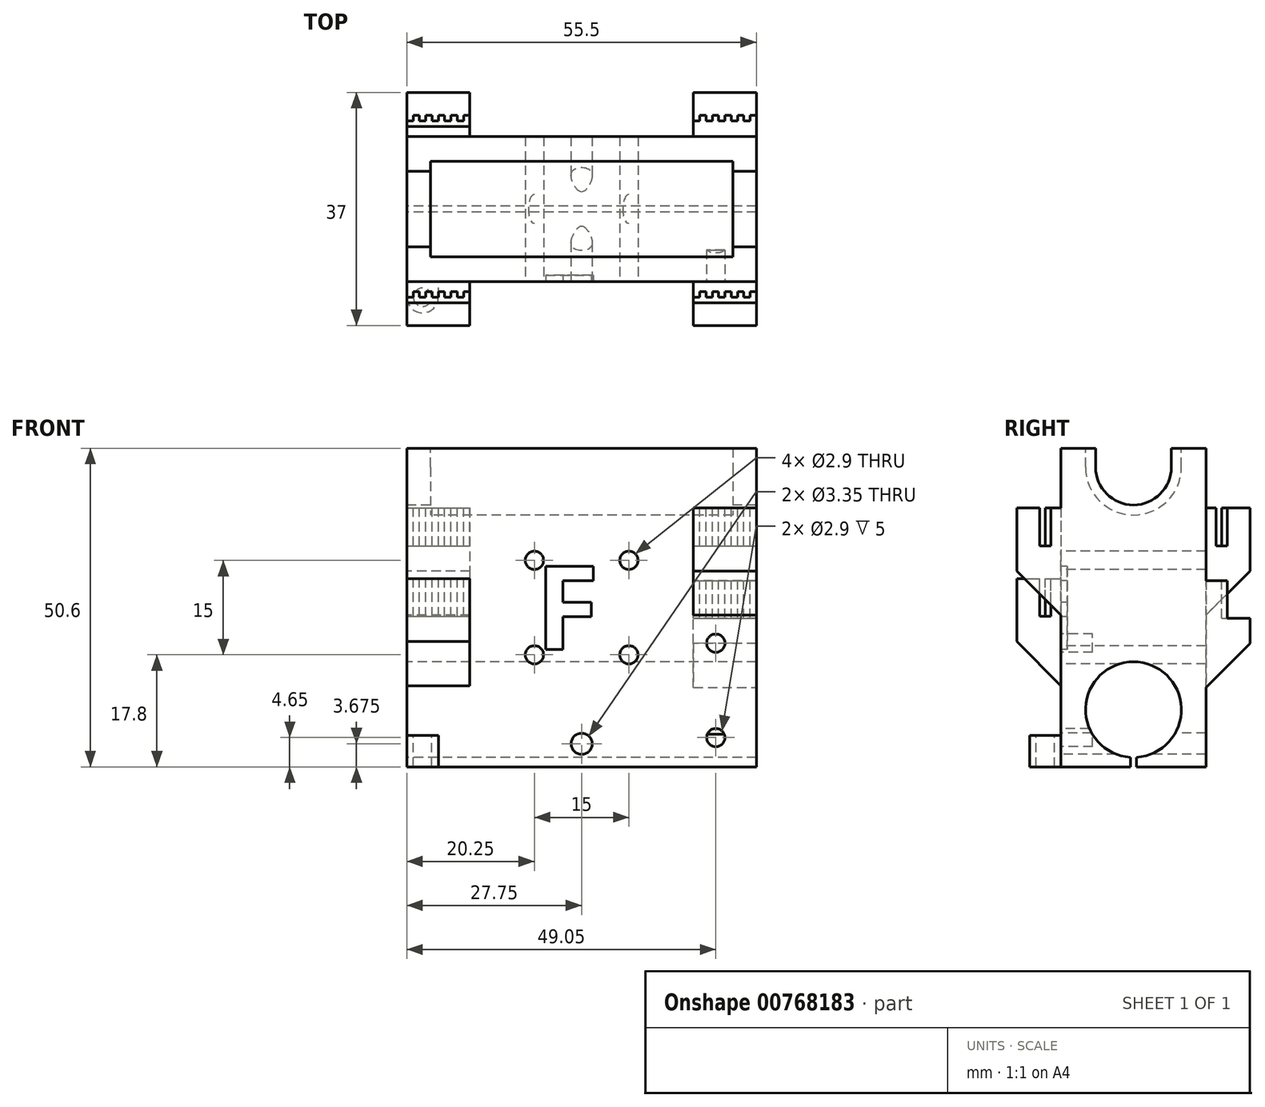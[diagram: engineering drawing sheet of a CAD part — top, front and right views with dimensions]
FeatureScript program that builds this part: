
annotation { "Feature Type Name" : "Feature", "Feature Type Description" : "" }
export const myFeature = defineFeature(function(context is Context, id is Id, definition is map)
    precondition{}
    {
        {
            assignVariable(context, id + "F0", {"name" : "LM8LUU", "anyValue" : 2.75});
        }
        {
            var Q0;
            Q0=qCreatedBy(makeId("Top.planeOp"),FACE);
            var sketch = newSketch(context, id + "F1", { "sketchPlane" : qUnion([Q0])});
            skLineSegment(sketch, "E0.bottom", {"start": v(0, 0) * mm, "end": v(55.5, 0) * mm});
            skLineSegment(sketch, "E0.top", {"start": v(0, 23) * mm, "end": v(55.5, 23) * mm});
            skLineSegment(sketch, "E0.left", {"start": v(0, 0) * mm, "end": v(0, 23) * mm});
            skLineSegment(sketch, "E0.right", {"start": v(55.5, 0) * mm, "end": v(55.5, 23) * mm});
            skSolve(sketch);
        }
        {
            var Q0;
            Q0=qSketchRegion(id+"F1",true);
            extrude(context, id + "F2", {"entities" : qUnion([Q0]), "depth" : 50.6 * mm});
        }
        {
            var Q0;
            Q0=makeQuery(id+"F2.opExtrude","SWEPT_FACE",FACE,{"disambiguationData":[OSD([sQuery(id+"F1.wireOp",EDGE,"E0.left")])]});
            var sketch = newSketch(context, id + "F3", { "sketchPlane" : qUnion([Q0])});
            skCircle(sketch, "E1", {"center": v(-11.5, 9.1) * mm, "radius": 7.6 * mm});
            skCircle(sketch, "E2", {"center": v(-11.5, 47.6) * mm, "radius": 6 * mm});
            skLineSegment(sketch, "E3", {"start": v(-23, 47.6) * mm, "end": v(0, 47.6) * mm, "construction": true});
            skLineSegment(sketch, "E4", {"start": v(-17.5, 50.6) * mm, "end": v(-17.5, 47.6) * mm});
            skLineSegment(sketch, "E5", {"start": v(-5.5, 50.6) * mm, "end": v(-5.5, 47.6) * mm});
            skLineSegment(sketch, "E6", {"start": v(-23, 9.1) * mm, "end": v(0, 9.1) * mm, "construction": true});
            skLineSegment(sketch, "E7", {"start": v(-11.5, 9.1) * mm, "end": v(-11.5, 0) * mm, "construction": true});
            skLineSegment(sketch, "E8", {"start": v(-11.5, 0) * mm, "end": v(-12, 0) * mm});
            skLineSegment(sketch, "E9", {"start": v(-12, 0) * mm, "end": v(-12, 1.52) * mm});
            skLineSegment(sketch, "E10", {"start": v(-12, 1.52) * mm, "end": v(-11, 1.52) * mm});
            skLineSegment(sketch, "E11", {"start": v(-11, 1.52) * mm, "end": v(-11, 0) * mm});
            skLineSegment(sketch, "E12", {"start": v(-11, 0) * mm, "end": v(-11.5, 0) * mm});
            skLineSegment(sketch, "E13", {"start": v(-11.5, 15.6) * mm, "end": v(-11.5, 16.7) * mm});
            skLineSegment(sketch, "E14", {"start": v(-11.5, 15.6) * mm, "end": v(-7, 15.22) * mm});
            skLineSegment(sketch, "E15", {"start": v(-11.5, 15.6) * mm, "end": v(-16, 15.22) * mm});
            skCircle(sketch, "E16", {"center": v(-11.5, 47.6) * mm, "radius": 7.6 * mm});
            skLineSegment(sketch, "E17", {"start": v(-3.9, 47.6) * mm, "end": v(-3.9, 50.6) * mm});
            skLineSegment(sketch, "E18", {"start": v(-19.1, 47.6) * mm, "end": v(-19.1, 50.6) * mm});
            skSolve(sketch);
        }
        {
            var Q0;
            {var subQ0=sQuery(id+"F3.wireOp",EDGE,"E14");var subQ1=sQuery(id+"F3.wireOp",EDGE,"E1");var subQ3=makeQuery(id+"F3.imprint","INTERSECT",VERTEX,{"disambiguationData":[OD(0.0)],"derivedFrom":[subQ1,subQ0]});Q0=makeQuery(id+"F3.imprint","IMPRINT",FACE,{"disambiguationData":[TD([[makeQuery(id+"F3.imprint","IMPRINT",EDGE,{"disambiguationData":[TD([[subQ3,-1.0]])],"derivedFrom":subQ1}),1.0]])]});}
            var Q1;
            {var subQ0=sQuery(id+"F3.wireOp",EDGE,"E15");var subQ1=sQuery(id+"F3.wireOp",EDGE,"E1");var subQ3=makeQuery(id+"F3.imprint","INTERSECT",VERTEX,{"disambiguationData":[OD(0.0)],"derivedFrom":[subQ1,subQ0]});Q1=makeQuery(id+"F3.imprint","IMPRINT",FACE,{"disambiguationData":[TD([[makeQuery(id+"F3.imprint","IMPRINT",EDGE,{"disambiguationData":[TD([[subQ3,1.0]])],"derivedFrom":subQ1}),1.0]])]});}
            var Q2;
            Q2=makeQuery(id+"F3.imprint","IMPRINT",FACE,{"disambiguationData":[TD([[makeQuery(id+"F3.imprint","IMPRINT",EDGE,{"derivedFrom":sQuery(id+"F3.wireOp",EDGE,"E8")}),-1.0]])]});
            var Q3;
            {var subQ0=sQuery(id+"F3.wireOp",EDGE,"E10");Q3=makeQuery(id+"F3.imprint","IMPRINT",FACE,{"disambiguationData":[TD([[makeQuery(id+"F3.imprint","IMPRINT",EDGE,{"derivedFrom":subQ0}),-1.0]])]});}
            var Q4;
            {var subQ3=sQuery(id+"F3.wireOp",EDGE,"E13");Q4=makeQuery(id+"F3.imprint","IMPRINT",FACE,{"disambiguationData":[TD([[makeQuery(id+"F3.imprint","IMPRINT",EDGE,{"derivedFrom":subQ3}),-1.0]])]});}
            var Q5;
            {var subQ3=sQuery(id+"F3.wireOp",EDGE,"E13");Q5=makeQuery(id+"F3.imprint","IMPRINT",FACE,{"disambiguationData":[TD([[makeQuery(id+"F3.imprint","IMPRINT",EDGE,{"derivedFrom":subQ3}),1.0]])]});}
            var Q6;
            {var subQ7=sQuery(id+"F3.wireOp",EDGE,"E10");Q6=makeQuery(id+"F3.imprint","IMPRINT",FACE,{"disambiguationData":[TD([[makeQuery(id+"F3.imprint","IMPRINT",EDGE,{"derivedFrom":subQ7}),1.0]])]});}
            var Q7;
            {var subQ3=sQuery(id+"F3.wireOp",EDGE,"E5");Q7=makeQuery(id+"F3.imprint","IMPRINT",FACE,{"disambiguationData":[TD([[makeQuery(id+"F3.imprint","IMPRINT",EDGE,{"derivedFrom":subQ3}),-1.0]])]});}
            var Q8;
            {var subQ0=sQuery(id+"F3.wireOp",EDGE,"E4");Q8=makeQuery(id+"F3.imprint","IMPRINT",FACE,{"disambiguationData":[TD([[makeQuery(id+"F3.imprint","IMPRINT",EDGE,{"derivedFrom":subQ0}),1.0]])]});}
            var Q9;
            {var subQ0=sQuery(id+"F3.wireOp",EDGE,"E4");Q9=makeQuery(id+"F3.imprint","IMPRINT",FACE,{"disambiguationData":[TD([[makeQuery(id+"F3.imprint","IMPRINT",EDGE,{"derivedFrom":subQ0}),1.0]])]});}
            var Q10;
            {var subQ3=sQuery(id+"F3.wireOp",EDGE,"E5");Q10=makeQuery(id+"F3.imprint","IMPRINT",FACE,{"disambiguationData":[TD([[makeQuery(id+"F3.imprint","IMPRINT",EDGE,{"derivedFrom":subQ3}),-1.0]])]});}
            var Q11;
            {var subQ1=sQuery(id+"F3.wireOp",EDGE,"E2");var subQ4=makeQuery(id+"F3.imprint","INTERSECT",VERTEX,{"derivedFrom":[subQ1,sQuery(id+"F3.wireOp",EDGE,"E5")]});Q11=makeQuery(id+"F3.imprint","IMPRINT",FACE,{"disambiguationData":[TD([[makeQuery(id+"F3.imprint","IMPRINT",EDGE,{"disambiguationData":[TD([[subQ4,-1.0]])],"derivedFrom":subQ1}),1.0]])]});}
            extrude(context, id + "F4", {"entities" : qUnion([Q0, Q1, Q2, Q3, Q4, Q5, Q6, Q7, Q8, Q9, Q10, Q11]), "operationType" : NewBodyOperationType.REMOVE, "endBound" : BoundingType.THROUGH_ALL, "oppositeDirection" : true, "depth" : 25 * mm});
        }
        {
            var Q0;
            {var subQ3=sQuery(id+"F3.wireOp",EDGE,"E4");Q0=makeQuery(id+"F3.imprint","IMPRINT",FACE,{"disambiguationData":[TD([[makeQuery(id+"F3.imprint","IMPRINT",EDGE,{"derivedFrom":subQ3}),-1.0]])]});}
            var Q1;
            {var subQ3=sQuery(id+"F3.wireOp",EDGE,"E18");Q1=makeQuery(id+"F3.imprint","IMPRINT",FACE,{"disambiguationData":[TD([[makeQuery(id+"F3.imprint","IMPRINT",EDGE,{"derivedFrom":subQ3}),-1.0]])]});}
            var Q2;
            {var subQ3=sQuery(id+"F3.wireOp",EDGE,"E17");Q2=makeQuery(id+"F3.imprint","IMPRINT",FACE,{"disambiguationData":[TD([[makeQuery(id+"F3.imprint","IMPRINT",EDGE,{"derivedFrom":subQ3}),1.0]])]});}
            extrude(context, id + "F5", {"entities" : qUnion([Q0, Q1, Q2]), "operationType" : NewBodyOperationType.REMOVE, "oppositeDirection" : true, "depth" : (46.25 + getVariable(context, 'LM8LUU') * 2) * mm, "offsetDistance" : 25 * mm});
        }
        {
            var Q0;
            {var subQ3=sQuery(id+"F3.wireOp",EDGE,"E4");Q0=makeQuery(id+"F3.imprint","IMPRINT",FACE,{"disambiguationData":[TD([[makeQuery(id+"F3.imprint","IMPRINT",EDGE,{"derivedFrom":subQ3}),-1.0]])]});}
            var Q1;
            {var subQ3=sQuery(id+"F3.wireOp",EDGE,"E18");Q1=makeQuery(id+"F3.imprint","IMPRINT",FACE,{"disambiguationData":[TD([[makeQuery(id+"F3.imprint","IMPRINT",EDGE,{"derivedFrom":subQ3}),-1.0]])]});}
            var Q2;
            {var subQ3=sQuery(id+"F3.wireOp",EDGE,"E17");Q2=makeQuery(id+"F3.imprint","IMPRINT",FACE,{"disambiguationData":[TD([[makeQuery(id+"F3.imprint","IMPRINT",EDGE,{"derivedFrom":subQ3}),1.0]])]});}
            extrude(context, id + "F6", {"entities" : qUnion([Q0, Q1, Q2]), "operationType" : NewBodyOperationType.ADD, "oppositeDirection" : true, "depth" : (26.75 - getVariable(context, 'LM8LUU')) * mm});
        }
        {
            var Q0;
            {var subQ3=sQuery(id+"F3.wireOp",EDGE,"E4");Q0=makeQuery(id+"F3.imprint","IMPRINT",FACE,{"disambiguationData":[TD([[makeQuery(id+"F3.imprint","IMPRINT",EDGE,{"derivedFrom":subQ3}),-1.0]])]});}
            var Q1;
            {var subQ3=sQuery(id+"F3.wireOp",EDGE,"E18");Q1=makeQuery(id+"F3.imprint","IMPRINT",FACE,{"disambiguationData":[TD([[makeQuery(id+"F3.imprint","IMPRINT",EDGE,{"derivedFrom":subQ3}),-1.0]])]});}
            var Q2;
            {var subQ3=sQuery(id+"F3.wireOp",EDGE,"E17");Q2=makeQuery(id+"F3.imprint","IMPRINT",FACE,{"disambiguationData":[TD([[makeQuery(id+"F3.imprint","IMPRINT",EDGE,{"derivedFrom":subQ3}),1.0]])]});}
            extrude(context, id + "F7", {"entities" : qUnion([Q0, Q1, Q2]), "operationType" : NewBodyOperationType.REMOVE, "oppositeDirection" : true, "depth" : (23.25 + getVariable(context, 'LM8LUU')) * mm});
        }
        {
            var Q0;
            {var subQ3=sQuery(id+"F3.wireOp",EDGE,"E4");Q0=makeQuery(id+"F3.imprint","IMPRINT",FACE,{"disambiguationData":[TD([[makeQuery(id+"F3.imprint","IMPRINT",EDGE,{"derivedFrom":subQ3}),-1.0]])]});}
            var Q1;
            {var subQ3=sQuery(id+"F3.wireOp",EDGE,"E18");Q1=makeQuery(id+"F3.imprint","IMPRINT",FACE,{"disambiguationData":[TD([[makeQuery(id+"F3.imprint","IMPRINT",EDGE,{"derivedFrom":subQ3}),-1.0]])]});}
            var Q2;
            {var subQ3=sQuery(id+"F3.wireOp",EDGE,"E17");Q2=makeQuery(id+"F3.imprint","IMPRINT",FACE,{"disambiguationData":[TD([[makeQuery(id+"F3.imprint","IMPRINT",EDGE,{"derivedFrom":subQ3}),1.0]])]});}
            extrude(context, id + "F8", {"entities" : qUnion([Q0, Q1, Q2]), "operationType" : NewBodyOperationType.ADD, "oppositeDirection" : true, "depth" : 3.75 * mm, "offsetDistance" : 25 * mm});
        }
        {
            var Q0;
            Q0=makeQuery(id+"F2.opExtrude","SWEPT_FACE",FACE,{"disambiguationData":[OSD([sQuery(id+"F1.wireOp",EDGE,"E0.bottom")])]});
            var sketch = newSketch(context, id + "F9", { "sketchPlane" : qUnion([Q0])});
            skLineSegment(sketch, "E19.bottom", {"start": v(0, 29.9) * mm, "end": v(10, 29.9) * mm});
            skLineSegment(sketch, "E19.top", {"start": v(0, 9.9) * mm, "end": v(10, 9.9) * mm});
            skLineSegment(sketch, "E19.left", {"start": v(0, 29.9) * mm, "end": v(0, 9.9) * mm});
            skLineSegment(sketch, "E19.right", {"start": v(10, 29.9) * mm, "end": v(10, 9.9) * mm});
            skLineSegment(sketch, "E20.bottom", {"start": v(55.5, 41.1) * mm, "end": v(45.5, 41.1) * mm});
            skLineSegment(sketch, "E20.top", {"start": v(55.5, 21.1) * mm, "end": v(45.5, 21.1) * mm});
            skLineSegment(sketch, "E20.left", {"start": v(55.5, 41.1) * mm, "end": v(55.5, 21.1) * mm});
            skLineSegment(sketch, "E20.right", {"start": v(45.5, 41.1) * mm, "end": v(45.5, 21.1) * mm});
            skPoint(sketch, "E21", {"position": v(0, 47.6) * mm});
            skPoint(sketch, "E22", {"position": v(0, 9.4) * mm});
            skSolve(sketch);
        }
        {
            var Q0;
            Q0=qSketchRegion(id+"F9",true);
            extrude(context, id + "F10", {"entities" : qUnion([Q0]), "operationType" : NewBodyOperationType.ADD, "depth" : 7 * mm});
        }
        {
            var Q0;
            Q0=makeQuery(id+"F10.opExtrude","CAP_EDGE",EDGE,{"disambiguationData":[OSD([sQuery(id+"F9.wireOp",EDGE,"E19.top")])],"isStart":false});
            var Q1;
            Q1=makeQuery(id+"F10.opExtrude","CAP_EDGE",EDGE,{"disambiguationData":[OSD([sQuery(id+"F9.wireOp",EDGE,"E20.top")])],"isStart":false});
            chamfer(context, id + "F11", {"entities" : qUnion([Q0, Q1]), "width" : 10 * mm, "tangentPropagation" : true});
        }
        {
            var Q0;
            Q0=makeQuery(id+"F10.opExtrude","SWEPT_FACE",FACE,{"disambiguationData":[OSD([sQuery(id+"F9.wireOp",EDGE,"E19.bottom")])]});
            var sketch = newSketch(context, id + "F12", { "sketchPlane" : qUnion([Q0])});
            skLineSegment(sketch, "E23", {"start": v(-935.9, 0) * mm, "end": v(-935.88, -4.54) * mm});
            skLineSegment(sketch, "E24.left", {"start": v(0, -3.4) * mm, "end": v(0, -1.6) * mm});
            skLineSegment(sketch, "E25", {"start": v(6, -2.5) * mm, "end": v(7, -2.5) * mm});
            skLineSegment(sketch, "E26", {"start": v(4, -2.5) * mm, "end": v(5, -2.5) * mm});
            skLineSegment(sketch, "E27", {"start": v(0, -2.5) * mm, "end": v(1, -2.5) * mm});
            skLineSegment(sketch, "E28", {"start": v(7, -1.6) * mm, "end": v(8, -1.6) * mm});
            skLineSegment(sketch, "E29", {"start": v(2, -2.5) * mm, "end": v(3, -2.5) * mm});
            skLineSegment(sketch, "E30", {"start": v(3, -1.6) * mm, "end": v(4, -1.6) * mm});
            skLineSegment(sketch, "E31", {"start": v(8, -2.5) * mm, "end": v(9, -2.5) * mm});
            skLineSegment(sketch, "E32", {"start": v(8, -1.6) * mm, "end": v(8, -2.5) * mm});
            skLineSegment(sketch, "E33", {"start": v(9, -2.5) * mm, "end": v(9, -1.6) * mm});
            skLineSegment(sketch, "E34", {"start": v(10, -1.6) * mm, "end": v(10, -2.5) * mm});
            skLineSegment(sketch, "E35", {"start": v(6, -1.6) * mm, "end": v(6, -2.5) * mm});
            skLineSegment(sketch, "E36", {"start": v(2, -1.6) * mm, "end": v(2, -2.5) * mm});
            skLineSegment(sketch, "E37", {"start": v(1, -1.6) * mm, "end": v(2, -1.6) * mm});
            skLineSegment(sketch, "E38", {"start": v(1, -2.5) * mm, "end": v(1, -1.6) * mm});
            skLineSegment(sketch, "E39", {"start": v(9, -1.6) * mm, "end": v(10, -1.6) * mm});
            skLineSegment(sketch, "E40", {"start": v(5, -1.6) * mm, "end": v(6, -1.6) * mm});
            skLineSegment(sketch, "E41", {"start": v(5, -2.5) * mm, "end": v(5, -1.6) * mm});
            skLineSegment(sketch, "E42", {"start": v(3, -2.5) * mm, "end": v(3, -1.6) * mm});
            skLineSegment(sketch, "E43", {"start": v(4, -1.6) * mm, "end": v(4, -2.5) * mm});
            skLineSegment(sketch, "E44", {"start": v(7, -2.5) * mm, "end": v(7, -1.6) * mm});
            skLineSegment(sketch, "E45", {"start": v(0, -1.6) * mm, "end": v(0, -2.5) * mm});
            skLineSegment(sketch, "E46", {"start": v(10, -2.5) * mm, "end": v(10, -3.4) * mm});
            skLineSegment(sketch, "E47", {"start": v(0, -3.4) * mm, "end": v(10, -3.4) * mm});
            skLineSegment(sketch, "E48", {"start": v(5.3, -1.6) * mm, "end": v(5.3, 0) * mm});
            skSolve(sketch);
        }
        {
            var Q0;
            Q0=qSketchRegion(id+"F12",true);
            extrude(context, id + "F13", {"entities" : qUnion([Q0]), "operationType" : NewBodyOperationType.REMOVE, "oppositeDirection" : true, "depth" : 6 * mm});
        }
        {
            var Q0;
            Q0=makeQuery(id+"F10.opExtrude","SWEPT_FACE",FACE,{"disambiguationData":[OSD([sQuery(id+"F9.wireOp",EDGE,"E20.bottom")])]});
            var sketch = newSketch(context, id + "F14", { "sketchPlane" : qUnion([Q0])});
            skLineSegment(sketch, "E49.left", {"start": v(45.5, -3.4) * mm, "end": v(45.5, -1.6) * mm});
            skLineSegment(sketch, "E50", {"start": v(51.5, -2.5) * mm, "end": v(52.5, -2.5) * mm});
            skLineSegment(sketch, "E51", {"start": v(49.5, -2.5) * mm, "end": v(50.5, -2.5) * mm});
            skLineSegment(sketch, "E52", {"start": v(45.5, -2.5) * mm, "end": v(46.5, -2.5) * mm});
            skLineSegment(sketch, "E53", {"start": v(52.5, -1.6) * mm, "end": v(53.5, -1.6) * mm});
            skLineSegment(sketch, "E54", {"start": v(47.5, -2.5) * mm, "end": v(48.5, -2.5) * mm});
            skLineSegment(sketch, "E55", {"start": v(48.5, -1.6) * mm, "end": v(49.5, -1.6) * mm});
            skLineSegment(sketch, "E56", {"start": v(53.5, -2.5) * mm, "end": v(54.5, -2.5) * mm});
            skLineSegment(sketch, "E57", {"start": v(53.5, -1.6) * mm, "end": v(53.5, -2.5) * mm});
            skLineSegment(sketch, "E58", {"start": v(54.5, -2.5) * mm, "end": v(54.5, -1.6) * mm});
            skLineSegment(sketch, "E59", {"start": v(55.5, -1.6) * mm, "end": v(55.5, -2.5) * mm});
            skLineSegment(sketch, "E60", {"start": v(51.5, -1.6) * mm, "end": v(51.5, -2.5) * mm});
            skLineSegment(sketch, "E61", {"start": v(47.5, -1.6) * mm, "end": v(47.5, -2.5) * mm});
            skLineSegment(sketch, "E62", {"start": v(46.5, -1.6) * mm, "end": v(47.5, -1.6) * mm});
            skLineSegment(sketch, "E63", {"start": v(46.5, -2.5) * mm, "end": v(46.5, -1.6) * mm});
            skLineSegment(sketch, "E64", {"start": v(54.5, -1.6) * mm, "end": v(55.5, -1.6) * mm});
            skLineSegment(sketch, "E65", {"start": v(50.5, -1.6) * mm, "end": v(51.5, -1.6) * mm});
            skLineSegment(sketch, "E66", {"start": v(50.5, -2.5) * mm, "end": v(50.5, -1.6) * mm});
            skLineSegment(sketch, "E67", {"start": v(48.5, -2.5) * mm, "end": v(48.5, -1.6) * mm});
            skLineSegment(sketch, "E68", {"start": v(49.5, -1.6) * mm, "end": v(49.5, -2.5) * mm});
            skLineSegment(sketch, "E69", {"start": v(52.5, -2.5) * mm, "end": v(52.5, -1.6) * mm});
            skLineSegment(sketch, "E70", {"start": v(45.5, -1.6) * mm, "end": v(45.5, -2.5) * mm});
            skLineSegment(sketch, "E71", {"start": v(55.5, -2.5) * mm, "end": v(55.5, -3.4) * mm});
            skLineSegment(sketch, "E72", {"start": v(45.5, -3.4) * mm, "end": v(55.5, -3.4) * mm});
            skLineSegment(sketch, "E73", {"start": v(50.73, -1.6) * mm, "end": v(50.73, 0) * mm});
            skSolve(sketch);
        }
        {
            var Q0;
            Q0=qSketchRegion(id+"F14",true);
            extrude(context, id + "F15", {"entities" : qUnion([Q0]), "operationType" : NewBodyOperationType.REMOVE, "oppositeDirection" : true, "depth" : 6 * mm});
        }
        {
            var Q0;
            Q0=makeQuery(id+"F2.opExtrude","SWEPT_FACE",FACE,{"disambiguationData":[OSD([sQuery(id+"F1.wireOp",EDGE,"E0.top")])]});
            var sketch = newSketch(context, id + "F16", { "sketchPlane" : qUnion([Q0])});
            skLineSegment(sketch, "E74.bottom", {"start": v(-55.5, 9.6) * mm, "end": v(-45.5, 9.6) * mm});
            skLineSegment(sketch, "E74.top", {"start": v(-55.5, 29.6) * mm, "end": v(-45.5, 29.6) * mm});
            skLineSegment(sketch, "E74.left", {"start": v(-55.5, 9.6) * mm, "end": v(-55.5, 29.6) * mm});
            skLineSegment(sketch, "E74.right", {"start": v(-45.5, 9.6) * mm, "end": v(-45.5, 29.6) * mm});
            skLineSegment(sketch, "E75.bottom", {"start": v(0, 41.1) * mm, "end": v(-10, 41.1) * mm});
            skLineSegment(sketch, "E75.top", {"start": v(0, 21.1) * mm, "end": v(-10, 21.1) * mm});
            skLineSegment(sketch, "E75.left", {"start": v(0, 41.1) * mm, "end": v(0, 21.1) * mm});
            skLineSegment(sketch, "E75.right", {"start": v(-10, 41.1) * mm, "end": v(-10, 21.1) * mm});
            skSolve(sketch);
        }
        {
            var Q0;
            Q0=qSketchRegion(id+"F16",true);
            extrude(context, id + "F17", {"entities" : qUnion([Q0]), "operationType" : NewBodyOperationType.ADD, "depth" : 7 * mm});
        }
        {
            var Q0;
            Q0=makeQuery(id+"F17.opExtrude","SWEPT_FACE",FACE,{"disambiguationData":[OSD([sQuery(id+"F16.wireOp",EDGE,"E74.top")])]});
            var sketch = newSketch(context, id + "F18", { "sketchPlane" : qUnion([Q0])});
            skLineSegment(sketch, "E76.left", {"start": v(45.5, 24.6) * mm, "end": v(45.5, 26.4) * mm});
            skLineSegment(sketch, "E77", {"start": v(51.5, 25.5) * mm, "end": v(52.5, 25.5) * mm});
            skLineSegment(sketch, "E78", {"start": v(49.5, 25.5) * mm, "end": v(50.5, 25.5) * mm});
            skLineSegment(sketch, "E79", {"start": v(45.5, 25.5) * mm, "end": v(46.5, 25.5) * mm});
            skLineSegment(sketch, "E80", {"start": v(52.5, 26.4) * mm, "end": v(53.5, 26.4) * mm});
            skLineSegment(sketch, "E81", {"start": v(47.5, 25.5) * mm, "end": v(48.5, 25.5) * mm});
            skLineSegment(sketch, "E82", {"start": v(48.5, 26.4) * mm, "end": v(49.5, 26.4) * mm});
            skLineSegment(sketch, "E83", {"start": v(53.5, 25.5) * mm, "end": v(54.5, 25.5) * mm});
            skLineSegment(sketch, "E84", {"start": v(53.5, 26.4) * mm, "end": v(53.5, 25.5) * mm});
            skLineSegment(sketch, "E85", {"start": v(54.5, 25.5) * mm, "end": v(54.5, 26.4) * mm});
            skLineSegment(sketch, "E86", {"start": v(55.5, 26.4) * mm, "end": v(55.5, 25.5) * mm});
            skLineSegment(sketch, "E87", {"start": v(51.5, 26.4) * mm, "end": v(51.5, 25.5) * mm});
            skLineSegment(sketch, "E88", {"start": v(47.5, 26.4) * mm, "end": v(47.5, 25.5) * mm});
            skLineSegment(sketch, "E89", {"start": v(46.5, 26.4) * mm, "end": v(47.5, 26.4) * mm});
            skLineSegment(sketch, "E90", {"start": v(46.5, 25.5) * mm, "end": v(46.5, 26.4) * mm});
            skLineSegment(sketch, "E91", {"start": v(54.5, 26.4) * mm, "end": v(55.5, 26.4) * mm});
            skLineSegment(sketch, "E92", {"start": v(50.5, 26.4) * mm, "end": v(51.5, 26.4) * mm});
            skLineSegment(sketch, "E93", {"start": v(50.5, 25.5) * mm, "end": v(50.5, 26.4) * mm});
            skLineSegment(sketch, "E94", {"start": v(48.5, 25.5) * mm, "end": v(48.5, 26.4) * mm});
            skLineSegment(sketch, "E95", {"start": v(49.5, 26.4) * mm, "end": v(49.5, 25.5) * mm});
            skLineSegment(sketch, "E96", {"start": v(52.5, 25.5) * mm, "end": v(52.5, 26.4) * mm});
            skLineSegment(sketch, "E97", {"start": v(45.5, 26.4) * mm, "end": v(45.5, 25.5) * mm});
            skLineSegment(sketch, "E98", {"start": v(55.5, 25.5) * mm, "end": v(55.5, 24.6) * mm});
            skLineSegment(sketch, "E99", {"start": v(45.5, 24.6) * mm, "end": v(55.5, 24.6) * mm});
            skLineSegment(sketch, "E100", {"start": v(50.5, 24.6) * mm, "end": v(50.5, 23) * mm});
            skSolve(sketch);
        }
        {
            var Q0;
            {var subQ4=sQuery(id+"F18.wireOp",EDGE,"E76.left");Q0=makeQuery(id+"F18.imprint","IMPRINT",FACE,{"disambiguationData":[TD([[makeQuery(id+"F18.imprint","IMPRINT",EDGE,{"derivedFrom":subQ4}),1.0]])]});}
            extrude(context, id + "F19", {"entities" : qUnion([Q0]), "operationType" : NewBodyOperationType.REMOVE, "oppositeDirection" : true, "depth" : 6 * mm});
        }
        {
            var Q0;
            Q0=makeQuery(id+"F17.opExtrude","SWEPT_FACE",FACE,{"disambiguationData":[OSD([sQuery(id+"F16.wireOp",EDGE,"E75.bottom")])]});
            var sketch = newSketch(context, id + "F20", { "sketchPlane" : qUnion([Q0])});
            skLineSegment(sketch, "E101", {"start": v(6, 25.5) * mm, "end": v(7, 25.5) * mm});
            skLineSegment(sketch, "E102", {"start": v(4, 25.5) * mm, "end": v(5, 25.5) * mm});
            skLineSegment(sketch, "E103", {"start": v(0, 25.5) * mm, "end": v(1, 25.5) * mm});
            skLineSegment(sketch, "E104", {"start": v(7, 26.4) * mm, "end": v(8, 26.4) * mm});
            skLineSegment(sketch, "E105", {"start": v(2, 25.5) * mm, "end": v(3, 25.5) * mm});
            skLineSegment(sketch, "E106", {"start": v(3, 26.4) * mm, "end": v(4, 26.4) * mm});
            skLineSegment(sketch, "E107", {"start": v(8, 25.5) * mm, "end": v(9, 25.5) * mm});
            skLineSegment(sketch, "E108", {"start": v(8, 26.4) * mm, "end": v(8, 25.5) * mm});
            skLineSegment(sketch, "E109", {"start": v(9, 25.5) * mm, "end": v(9, 26.4) * mm});
            skLineSegment(sketch, "E110", {"start": v(10, 26.4) * mm, "end": v(10, 25.5) * mm});
            skLineSegment(sketch, "E111", {"start": v(6, 26.4) * mm, "end": v(6, 25.5) * mm});
            skLineSegment(sketch, "E112", {"start": v(2, 26.4) * mm, "end": v(2, 25.5) * mm});
            skLineSegment(sketch, "E113", {"start": v(1, 26.4) * mm, "end": v(2, 26.4) * mm});
            skLineSegment(sketch, "E114", {"start": v(1, 25.5) * mm, "end": v(1, 26.4) * mm});
            skLineSegment(sketch, "E115", {"start": v(9, 26.4) * mm, "end": v(10, 26.4) * mm});
            skLineSegment(sketch, "E116", {"start": v(5, 26.4) * mm, "end": v(6, 26.4) * mm});
            skLineSegment(sketch, "E117", {"start": v(5, 25.5) * mm, "end": v(5, 26.4) * mm});
            skLineSegment(sketch, "E118", {"start": v(3, 25.5) * mm, "end": v(3, 26.4) * mm});
            skLineSegment(sketch, "E119", {"start": v(4, 26.4) * mm, "end": v(4, 25.5) * mm});
            skLineSegment(sketch, "E120", {"start": v(7, 25.5) * mm, "end": v(7, 26.4) * mm});
            skLineSegment(sketch, "E121", {"start": v(10, 25.5) * mm, "end": v(10, 24.6) * mm});
            skLineSegment(sketch, "E122", {"start": v(0, 24.6) * mm, "end": v(10, 24.6) * mm});
            skLineSegment(sketch, "E123", {"start": v(5, 24.6) * mm, "end": v(5, 23) * mm});
            skLineSegment(sketch, "E124", {"start": v(0, 24.6) * mm, "end": v(0, 25.5) * mm});
            skSolve(sketch);
        }
        {
            var Q0;
            Q0=makeQuery(id+"F20.imprint","IMPRINT",FACE,{"disambiguationData":[TD([[makeQuery(id+"F20.imprint","IMPRINT",EDGE,{"derivedFrom":sQuery(id+"F20.wireOp",EDGE,"E101")}),-1.0]])]});
            extrude(context, id + "F21", {"entities" : qUnion([Q0]), "operationType" : NewBodyOperationType.REMOVE, "oppositeDirection" : true, "depth" : 6 * mm});
        }
        {
            var Q0;
            Q0=makeQuery(id+"F17.opExtrude","CAP_EDGE",EDGE,{"disambiguationData":[OSD([sQuery(id+"F16.wireOp",EDGE,"E75.top")])],"isStart":false});
            var Q1;
            Q1=makeQuery(id+"F17.opExtrude","CAP_EDGE",EDGE,{"disambiguationData":[OSD([sQuery(id+"F16.wireOp",EDGE,"E74.bottom")])],"isStart":false});
            chamfer(context, id + "F22", {"entities" : qUnion([Q0, Q1]), "width" : 10 * mm, "tangentPropagation" : true});
        }
        {
            var Q0;
            Q0=makeQuery(id+"F2.opExtrude","SWEPT_FACE",FACE,{"disambiguationData":[OSD([sQuery(id+"F1.wireOp",EDGE,"E0.bottom")])]});
            var sketch = newSketch(context, id + "F23", { "sketchPlane" : qUnion([Q0])});
            skCircle(sketch, "E125", {"center": v(20.25, 32.8) * mm, "radius": 1.45 * mm});
            skCircle(sketch, "E126", {"center": v(35.25, 32.8) * mm, "radius": 1.45 * mm});
            skCircle(sketch, "E127", {"center": v(20.25, 17.8) * mm, "radius": 1.45 * mm});
            skCircle(sketch, "E128", {"center": v(35.25, 17.8) * mm, "radius": 1.45 * mm});
            skLineSegment(sketch, "E129", {"start": v(20.25, 32.8) * mm, "end": v(0, 32.8) * mm});
            skLineSegment(sketch, "E130", {"start": v(35.25, 17.8) * mm, "end": v(55.5, 17.8) * mm});
            skLineSegment(sketch, "E131", {"start": v(35.25, 32.8) * mm, "end": v(35.25, 50.6) * mm});
            skLineSegment(sketch, "E132", {"start": v(20.25, 17.8) * mm, "end": v(20.25, 0) * mm});
            skCircle(sketch, "E133", {"center": v(27.75, 3.68) * mm, "radius": 1.68 * mm});
            skLineSegment(sketch, "E134", {"start": v(27.75, 0) * mm, "end": v(27.75, 13.82) * mm, "construction": true});
            skSolve(sketch);
        }
        {
            var Q0;
            Q0=qSketchRegion(id+"F23",true);
            var Q1;
            Q1=makeQuery(id+"F23.imprint","IMPRINT",FACE,{"disambiguationData":[TD([[makeQuery(id+"F23.imprint","IMPRINT",EDGE,{"derivedFrom":sQuery(id+"F23.wireOp",EDGE,"E125")}),1.0]])]});
            var Q2;
            Q2=makeQuery(id+"F23.imprint","IMPRINT",FACE,{"disambiguationData":[TD([[makeQuery(id+"F23.imprint","IMPRINT",EDGE,{"derivedFrom":sQuery(id+"F23.wireOp",EDGE,"E126")}),1.0]])]});
            var Q3;
            Q3=makeQuery(id+"F23.imprint","IMPRINT",FACE,{"disambiguationData":[TD([[makeQuery(id+"F23.imprint","IMPRINT",EDGE,{"derivedFrom":sQuery(id+"F23.wireOp",EDGE,"E128")}),1.0]])]});
            var Q4;
            Q4=makeQuery(id+"F23.imprint","IMPRINT",FACE,{"disambiguationData":[TD([[makeQuery(id+"F23.imprint","IMPRINT",EDGE,{"derivedFrom":sQuery(id+"F23.wireOp",EDGE,"E127")}),1.0]])]});
            extrude(context, id + "F24", {"entities" : qUnion([Q0, Q1, Q2, Q3, Q4]), "operationType" : NewBodyOperationType.REMOVE, "endBound" : BoundingType.THROUGH_ALL, "oppositeDirection" : true, "depth" : 25 * mm});
        }
        {
            var Q0;
            Q0=makeQuery(id+"F2.opExtrude","SWEPT_FACE",FACE,{"disambiguationData":[OSD([sQuery(id+"F1.wireOp",EDGE,"E0.bottom")])]});
            var sketch = newSketch(context, id + "F25", { "sketchPlane" : qUnion([Q0])});
            skCircle(sketch, "E135", {"center": v(49.05, 19.65) * mm, "radius": 1.45 * mm});
            skCircle(sketch, "E136", {"center": v(49.05, 4.65) * mm, "radius": 1.45 * mm});
            skSolve(sketch);
        }
        {
            var Q0;
            Q0=qSketchRegion(id+"F25",true);
            extrude(context, id + "F26", {"entities" : qUnion([Q0]), "operationType" : NewBodyOperationType.REMOVE, "oppositeDirection" : true, "depth" : 5 * mm});
        }
        {
            var Q0;
            Q0=makeQuery(id+"F2.opExtrude","SWEPT_FACE",FACE,{"disambiguationData":[OSD([sQuery(id+"F1.wireOp",EDGE,"E0.bottom")])]});
            var sketch = newSketch(context, id + "F27", { "sketchPlane" : qUnion([Q0])});
            skText(sketch, "E137", { "text": "F", "fontName": "OpenSans-Bold.ttf"});
            skLineSegment(sketch, "E138", {"start": v(20.25, 32.8) * mm, "end": v(20.25, 17.8) * mm, "construction": true});
            skLineSegment(sketch, "E139", {"start": v(20.25, 17.8) * mm, "end": v(35.25, 17.8) * mm, "construction": true});
            skLineSegment(sketch, "E140", {"start": v(35.25, 17.8) * mm, "end": v(35.25, 32.8) * mm, "construction": true});
            skLineSegment(sketch, "E141", {"start": v(35.25, 32.8) * mm, "end": v(20.25, 32.8) * mm, "construction": true});
            skLineSegment(sketch, "E142", {"start": v(20.25, 25.3) * mm, "end": v(23.15, 25.3) * mm, "construction": true});
            skLineSegment(sketch, "E143", {"start": v(32.35, 25.3) * mm, "end": v(35.25, 25.3) * mm, "construction": true});
            skLineSegment(sketch, "E144", {"start": v(27.75, 18.66) * mm, "end": v(27.75, 17.8) * mm, "construction": true});
            skLineSegment(sketch, "E145", {"start": v(27.75, 32.8) * mm, "end": v(27.75, 31.94) * mm, "construction": true});
            const initialGuessF27  = {"E137": [0.0204, 0.01866, 1, 0, 0.01328]};
            skSetInitialGuess(sketch, initialGuessF27);
            skSolve(sketch);
        }
        {
            var Q0;
            Q0=qSketchRegion(id+"F27",true);
            extrude(context, id + "F28", {"entities" : qUnion([Q0]), "operationType" : NewBodyOperationType.REMOVE, "oppositeDirection" : true, "depth" : 1 * mm});
        }
        {
            var Q0;
            Q0=makeQuery(id+"F2.opExtrude","SWEPT_FACE",FACE,{"disambiguationData":[OSD([sQuery(id+"F1.wireOp",EDGE,"E0.bottom")])]});
            var sketch = newSketch(context, id + "F29", { "sketchPlane" : qUnion([Q0])});
            skLineSegment(sketch, "E146.bottom", {"start": v(0, 0) * mm, "end": v(5, 0) * mm});
            skLineSegment(sketch, "E146.top", {"start": v(0, 5) * mm, "end": v(5, 5) * mm});
            skLineSegment(sketch, "E146.left", {"start": v(0, 0) * mm, "end": v(0, 5) * mm});
            skLineSegment(sketch, "E146.right", {"start": v(5, 0) * mm, "end": v(5, 5) * mm});
            skSolve(sketch);
        }
        {
            var Q0;
            Q0=qSketchRegion(id+"F29",true);
            extrude(context, id + "F30", {"entities" : qUnion([Q0]), "operationType" : NewBodyOperationType.ADD, "depth" : 5 * mm});
        }
        {
            var Q0;
            Q0=makeQuery(id+"F30.opExtrude","SWEPT_FACE",FACE,{"disambiguationData":[OSD([sQuery(id+"F29.wireOp",EDGE,"E146.top")])]});
            var sketch = newSketch(context, id + "F31", { "sketchPlane" : qUnion([Q0])});
            skCircle(sketch, "E147", {"center": v(2.5, -2.5) * mm, "radius": 1.45 * mm});
            skLineSegment(sketch, "E148", {"start": v(0, -2.5) * mm, "end": v(5, -2.5) * mm});
            skSolve(sketch);
        }
        {
            var Q0;
            Q0=qSketchRegion(id+"F31",true);
            extrude(context, id + "F32", {"entities" : qUnion([Q0]), "operationType" : NewBodyOperationType.REMOVE, "oppositeDirection" : true, "depth" : 25 * mm});
        }
        {
            var Q0;
            Q0=makeQuery(id+"F30.opExtrude","CAP_EDGE",EDGE,{"disambiguationData":[OSD([sQuery(id+"F29.wireOp",EDGE,"E146.left")])],"isStart":false});
            var Q1;
            Q1=makeQuery(id+"F30.opExtrude","CAP_EDGE",EDGE,{"disambiguationData":[OSD([sQuery(id+"F29.wireOp",EDGE,"E146.right")])],"isStart":false});
            fillet(context, id + "F33", {"entities" : qUnion([Q0, Q1]), "radius" : 2.5 * mm, "tangentPropagation" : true, "allowEdgeOverflow" : false});
        }
    });
